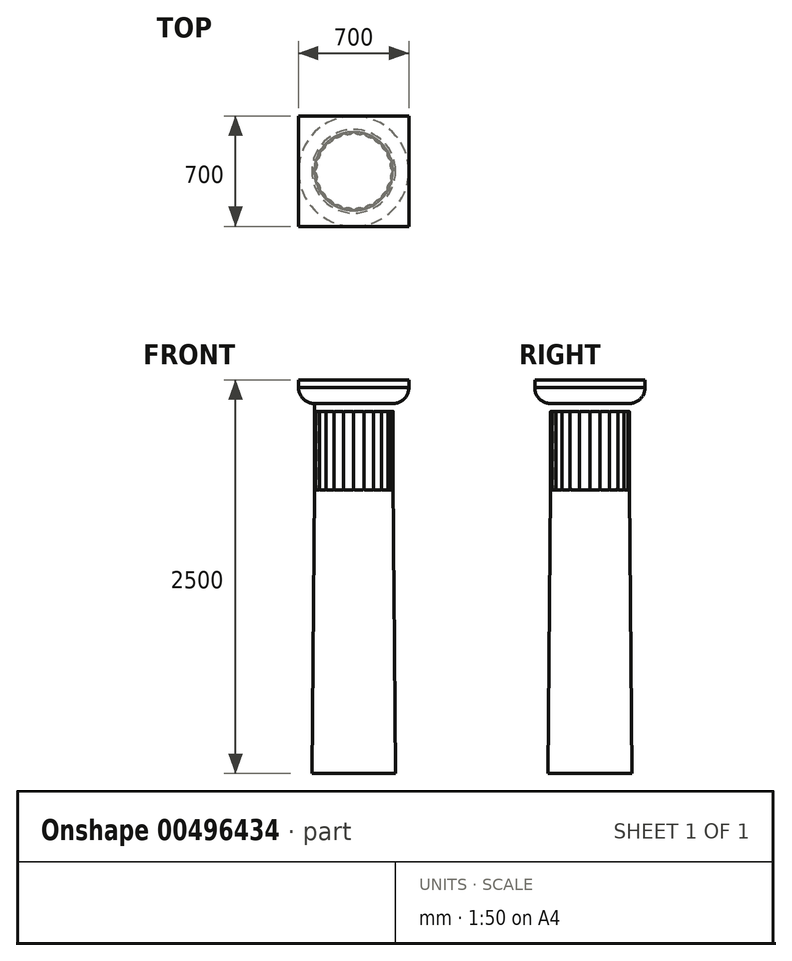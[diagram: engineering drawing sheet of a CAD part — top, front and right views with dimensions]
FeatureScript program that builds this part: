
annotation { "Feature Type Name" : "Feature", "Feature Type Description" : "" }
export const myFeature = defineFeature(function(context is Context, id is Id, definition is map)
    precondition{}
    {
        {
            var Q0;
            Q0=qCreatedBy(makeId("Top.planeOp"),FACE);
            var sketch = newSketch(context, id + "F0", { "sketchPlane" : qUnion([Q0])});
            skCircle(sketch, "E0", {"center": v(0, 0) * mm, "radius": 250 * mm});
            skArc(sketch, "E1", {"start": v(64.7, -241.48) * mm, "mid": v(30.88, -234.52) * mm, "end": v(0, -250) * mm});
            skLineSegment(sketch, "E2", {"start": v(0, 0) * mm, "end": v(30.88, -234.52) * mm, "construction": true});
            skLineSegment(sketch, "E3", {"start": v(30.88, -234.52) * mm, "end": v(32.63, -247.86) * mm, "construction": true});
            skArc(sketch, "E4.1.0", {"start": v(125, -216.5) * mm, "mid": v(90.52, -218.54) * mm, "end": v(64.7, -241.48) * mm});
            skArc(sketch, "E4.2.0", {"start": v(176.78, -176.78) * mm, "mid": v(144, -187.66) * mm, "end": v(125, -216.5) * mm});
            skArc(sketch, "E4.3.0", {"start": v(216.5, -125) * mm, "mid": v(187.66, -144) * mm, "end": v(176.78, -176.78) * mm});
            skArc(sketch, "E4.4.0", {"start": v(241.48, -64.7) * mm, "mid": v(218.54, -90.52) * mm, "end": v(216.5, -125) * mm});
            skArc(sketch, "E4.5.0", {"start": v(250, 0) * mm, "mid": v(234.52, -30.88) * mm, "end": v(241.48, -64.7) * mm});
            skArc(sketch, "E4.6.0", {"start": v(241.48, 64.7) * mm, "mid": v(234.52, 30.88) * mm, "end": v(250, 0) * mm});
            skArc(sketch, "E4.7.0", {"start": v(216.5, 125) * mm, "mid": v(218.54, 90.52) * mm, "end": v(241.48, 64.7) * mm});
            skArc(sketch, "E4.8.0", {"start": v(176.78, 176.78) * mm, "mid": v(187.66, 144) * mm, "end": v(216.5, 125) * mm});
            skArc(sketch, "E4.9.0", {"start": v(125, 216.5) * mm, "mid": v(144, 187.66) * mm, "end": v(176.78, 176.78) * mm});
            skArc(sketch, "E4.10.0", {"start": v(64.7, 241.48) * mm, "mid": v(90.52, 218.54) * mm, "end": v(125, 216.5) * mm});
            skArc(sketch, "E4.11.0", {"start": v(0, 250) * mm, "mid": v(30.88, 234.52) * mm, "end": v(64.7, 241.48) * mm});
            skArc(sketch, "E4.12.0", {"start": v(-64.7, 241.48) * mm, "mid": v(-30.88, 234.52) * mm, "end": v(0, 250) * mm});
            skArc(sketch, "E4.13.0", {"start": v(-125, 216.5) * mm, "mid": v(-90.52, 218.54) * mm, "end": v(-64.7, 241.48) * mm});
            skArc(sketch, "E4.14.0", {"start": v(-176.78, 176.78) * mm, "mid": v(-144, 187.66) * mm, "end": v(-125, 216.5) * mm});
            skArc(sketch, "E4.15.0", {"start": v(-216.5, 125) * mm, "mid": v(-187.66, 144) * mm, "end": v(-176.78, 176.78) * mm});
            skArc(sketch, "E4.16.0", {"start": v(-241.48, 64.7) * mm, "mid": v(-218.54, 90.52) * mm, "end": v(-216.5, 125) * mm});
            skArc(sketch, "E4.17.0", {"start": v(-250, 0) * mm, "mid": v(-234.52, 30.88) * mm, "end": v(-241.48, 64.7) * mm});
            skArc(sketch, "E4.18.0", {"start": v(-241.48, -64.7) * mm, "mid": v(-234.52, -30.88) * mm, "end": v(-250, 0) * mm});
            skArc(sketch, "E4.19.0", {"start": v(-216.5, -125) * mm, "mid": v(-218.54, -90.52) * mm, "end": v(-241.48, -64.7) * mm});
            skArc(sketch, "E4.20.0", {"start": v(-176.78, -176.78) * mm, "mid": v(-187.66, -144) * mm, "end": v(-216.5, -125) * mm});
            skArc(sketch, "E4.21.0", {"start": v(-125, -216.5) * mm, "mid": v(-144, -187.66) * mm, "end": v(-176.78, -176.78) * mm});
            skArc(sketch, "E4.22.0", {"start": v(-64.7, -241.48) * mm, "mid": v(-90.52, -218.54) * mm, "end": v(-125, -216.5) * mm});
            skArc(sketch, "E4.23.0", {"start": v(0, -250) * mm, "mid": v(-30.88, -234.52) * mm, "end": v(-64.7, -241.48) * mm});
            skSolve(sketch);
        }
        {
            var Q0;
            Q0=makeQuery(id+"F0.imprint","IMPRINT",FACE,{"disambiguationData":[TD([[makeQuery(id+"F0.imprint","IMPRINT",EDGE,{"derivedFrom":sQuery(id+"F0.wireOp",EDGE,"E1")}),-1.0]])]});
            extrude(context, id + "F1", {"entities" : qUnion([Q0]), "depth" : 500 * mm});
        }
        {
            var Q0;
            Q0 = qSketchRegion(id + "F0", true);
            extrude(context, id + "F2", {"entities" : qUnion([Q0]), "operationType" : NewBodyOperationType.ADD, "oppositeDirection" : true, "depth" : 1800 * mm, "hasDraft" : true, "draftAngle" : .5 * degree});
        }
        {
            var Q0;
            Q0=makeQuery(id+"F1.opExtrude","CAP_FACE",FACE,{"disambiguationData":[OSD([sQuery(id+"F0.wireOp",EDGE,"E1"),sQuery(id+"F0.wireOp",EDGE,"E4.1.0"),sQuery(id+"F0.wireOp",EDGE,"E4.2.0"),sQuery(id+"F0.wireOp",EDGE,"E4.3.0"),sQuery(id+"F0.wireOp",EDGE,"E4.4.0"),sQuery(id+"F0.wireOp",EDGE,"E4.5.0"),sQuery(id+"F0.wireOp",EDGE,"E4.6.0"),sQuery(id+"F0.wireOp",EDGE,"E4.7.0"),sQuery(id+"F0.wireOp",EDGE,"E4.8.0"),sQuery(id+"F0.wireOp",EDGE,"E4.9.0"),sQuery(id+"F0.wireOp",EDGE,"E4.10.0"),sQuery(id+"F0.wireOp",EDGE,"E4.11.0"),sQuery(id+"F0.wireOp",EDGE,"E4.12.0"),sQuery(id+"F0.wireOp",EDGE,"E4.13.0"),sQuery(id+"F0.wireOp",EDGE,"E4.14.0"),sQuery(id+"F0.wireOp",EDGE,"E4.15.0"),sQuery(id+"F0.wireOp",EDGE,"E4.16.0"),sQuery(id+"F0.wireOp",EDGE,"E4.17.0"),sQuery(id+"F0.wireOp",EDGE,"E4.18.0"),sQuery(id+"F0.wireOp",EDGE,"E4.19.0"),sQuery(id+"F0.wireOp",EDGE,"E4.20.0"),sQuery(id+"F0.wireOp",EDGE,"E4.21.0"),sQuery(id+"F0.wireOp",EDGE,"E4.22.0"),sQuery(id+"F0.wireOp",EDGE,"E4.23.0")])],"isStart":false});
            var sketch = newSketch(context, id + "F3", { "sketchPlane" : qUnion([Q0])});
            skCircle(sketch, "E5.0", {"center": v(0, 0) * mm, "radius": 250 * mm});
            skSolve(sketch);
        }
        {
            var Q0;
            Q0 = qSketchRegion(id + "F3", true);
            extrude(context, id + "F4", {"entities" : qUnion([Q0]), "operationType" : NewBodyOperationType.ADD, "depth" : 50 * mm});
        }
        {
            var Q0;
            Q0=makeQuery(id+"F4.opExtrude","CAP_FACE",FACE,{"disambiguationData":[OSD([sQuery(id+"F3.wireOp",EDGE,"E5.0")])],"isStart":false});
            var sketch = newSketch(context, id + "F5", { "sketchPlane" : qUnion([Q0])});
            skCircle(sketch, "E6", {"center": v(0, 0) * mm, "radius": 350 * mm});
            skSolve(sketch);
        }
        {
            var Q0;
            Q0 = qSketchRegion(id + "F5", true);
            extrude(context, id + "F6", {"entities" : qUnion([Q0]), "operationType" : NewBodyOperationType.ADD, "depth" : 100 * mm});
        }
        {
            var Q0;
            Q0=makeQuery(id+"F6.opExtrude","CAP_EDGE",EDGE,{"disambiguationData":[OSD([sQuery(id+"F5.wireOp",EDGE,"E6")])],"isStart":true});
            fillet(context, id + "F7", {"entities" : qUnion([Q0]), "radius" : 100 * mm, "tangentPropagation" : true, "allowEdgeOverflow" : false});
        }
        {
            var Q0;
            Q0=makeQuery(id+"F1.opExtrude","CAP_EDGE",EDGE,{"disambiguationData":[OSD([sQuery(id+"F0.wireOp",EDGE,"E4.20.0")])],"isStart":false});
            var Q1;
            Q1=makeQuery(id+"F1.opExtrude","CAP_EDGE",EDGE,{"disambiguationData":[OSD([sQuery(id+"F0.wireOp",EDGE,"E4.19.0")])],"isStart":false});
            var Q2;
            Q2=makeQuery(id+"F1.opExtrude","CAP_EDGE",EDGE,{"disambiguationData":[OSD([sQuery(id+"F0.wireOp",EDGE,"E4.18.0")])],"isStart":false});
            var Q3;
            Q3=makeQuery(id+"F1.opExtrude","CAP_EDGE",EDGE,{"disambiguationData":[OSD([sQuery(id+"F0.wireOp",EDGE,"E4.17.0")])],"isStart":false});
            var Q4;
            Q4=makeQuery(id+"F1.opExtrude","CAP_EDGE",EDGE,{"disambiguationData":[OSD([sQuery(id+"F0.wireOp",EDGE,"E4.21.0")])],"isStart":false});
            var Q5;
            Q5=makeQuery(id+"F1.opExtrude","CAP_EDGE",EDGE,{"disambiguationData":[OSD([sQuery(id+"F0.wireOp",EDGE,"E4.22.0")])],"isStart":false});
            var Q6;
            Q6=makeQuery(id+"F1.opExtrude","CAP_EDGE",EDGE,{"disambiguationData":[OSD([sQuery(id+"F0.wireOp",EDGE,"E4.23.0")])],"isStart":false});
            var Q7;
            Q7=makeQuery(id+"F1.opExtrude","CAP_EDGE",EDGE,{"disambiguationData":[OSD([sQuery(id+"F0.wireOp",EDGE,"E1")])],"isStart":false});
            var Q8;
            Q8=makeQuery(id+"F1.opExtrude","CAP_EDGE",EDGE,{"disambiguationData":[OSD([sQuery(id+"F0.wireOp",EDGE,"E4.1.0")])],"isStart":false});
            var Q9;
            Q9=makeQuery(id+"F1.opExtrude","CAP_EDGE",EDGE,{"disambiguationData":[OSD([sQuery(id+"F0.wireOp",EDGE,"E4.2.0")])],"isStart":false});
            var Q10;
            Q10=makeQuery(id+"F1.opExtrude","CAP_EDGE",EDGE,{"disambiguationData":[OSD([sQuery(id+"F0.wireOp",EDGE,"E4.3.0")])],"isStart":false});
            var Q11;
            Q11=makeQuery(id+"F1.opExtrude","CAP_EDGE",EDGE,{"disambiguationData":[OSD([sQuery(id+"F0.wireOp",EDGE,"E4.4.0")])],"isStart":false});
            var Q12;
            Q12=makeQuery(id+"F1.opExtrude","CAP_EDGE",EDGE,{"disambiguationData":[OSD([sQuery(id+"F0.wireOp",EDGE,"E4.5.0")])],"isStart":false});
            var Q13;
            Q13=makeQuery(id+"F1.opExtrude","CAP_EDGE",EDGE,{"disambiguationData":[OSD([sQuery(id+"F0.wireOp",EDGE,"E4.6.0")])],"isStart":false});
            var Q14;
            Q14=makeQuery(id+"F1.opExtrude","CAP_EDGE",EDGE,{"disambiguationData":[OSD([sQuery(id+"F0.wireOp",EDGE,"E4.7.0")])],"isStart":false});
            var Q15;
            Q15=makeQuery(id+"F1.opExtrude","CAP_EDGE",EDGE,{"disambiguationData":[OSD([sQuery(id+"F0.wireOp",EDGE,"E4.8.0")])],"isStart":false});
            var Q16;
            Q16=makeQuery(id+"F1.opExtrude","CAP_EDGE",EDGE,{"disambiguationData":[OSD([sQuery(id+"F0.wireOp",EDGE,"E4.9.0")])],"isStart":false});
            var Q17;
            Q17=makeQuery(id+"F1.opExtrude","CAP_EDGE",EDGE,{"disambiguationData":[OSD([sQuery(id+"F0.wireOp",EDGE,"E4.10.0")])],"isStart":false});
            var Q18;
            Q18=makeQuery(id+"F1.opExtrude","CAP_EDGE",EDGE,{"disambiguationData":[OSD([sQuery(id+"F0.wireOp",EDGE,"E4.11.0")])],"isStart":false});
            var Q19;
            Q19=makeQuery(id+"F1.opExtrude","CAP_EDGE",EDGE,{"disambiguationData":[OSD([sQuery(id+"F0.wireOp",EDGE,"E4.12.0")])],"isStart":false});
            var Q20;
            Q20=makeQuery(id+"F1.opExtrude","CAP_EDGE",EDGE,{"disambiguationData":[OSD([sQuery(id+"F0.wireOp",EDGE,"E4.13.0")])],"isStart":false});
            var Q21;
            Q21=makeQuery(id+"F1.opExtrude","CAP_EDGE",EDGE,{"disambiguationData":[OSD([sQuery(id+"F0.wireOp",EDGE,"E4.14.0")])],"isStart":false});
            var Q22;
            Q22=makeQuery(id+"F1.opExtrude","CAP_EDGE",EDGE,{"disambiguationData":[OSD([sQuery(id+"F0.wireOp",EDGE,"E4.15.0")])],"isStart":false});
            var Q23;
            Q23=makeQuery(id+"F1.opExtrude","CAP_EDGE",EDGE,{"disambiguationData":[OSD([sQuery(id+"F0.wireOp",EDGE,"E4.16.0")])],"isStart":false});
            var Q24;
            Q24=makeQuery(id+"F1.opExtrude","CAP_EDGE",EDGE,{"disambiguationData":[OSD([sQuery(id+"F0.wireOp",EDGE,"E4.11.0")])],"isStart":true});
            var Q25;
            Q25=makeQuery(id+"F1.opExtrude","CAP_EDGE",EDGE,{"disambiguationData":[OSD([sQuery(id+"F0.wireOp",EDGE,"E4.12.0")])],"isStart":true});
            var Q26;
            Q26=makeQuery(id+"F1.opExtrude","CAP_EDGE",EDGE,{"disambiguationData":[OSD([sQuery(id+"F0.wireOp",EDGE,"E4.13.0")])],"isStart":true});
            var Q27;
            Q27=makeQuery(id+"F1.opExtrude","CAP_EDGE",EDGE,{"disambiguationData":[OSD([sQuery(id+"F0.wireOp",EDGE,"E4.14.0")])],"isStart":true});
            var Q28;
            Q28=makeQuery(id+"F1.opExtrude","CAP_EDGE",EDGE,{"disambiguationData":[OSD([sQuery(id+"F0.wireOp",EDGE,"E4.15.0")])],"isStart":true});
            var Q29;
            Q29=makeQuery(id+"F1.opExtrude","CAP_EDGE",EDGE,{"disambiguationData":[OSD([sQuery(id+"F0.wireOp",EDGE,"E4.16.0")])],"isStart":true});
            var Q30;
            Q30=makeQuery(id+"F1.opExtrude","CAP_EDGE",EDGE,{"disambiguationData":[OSD([sQuery(id+"F0.wireOp",EDGE,"E4.10.0")])],"isStart":true});
            var Q31;
            Q31=makeQuery(id+"F1.opExtrude","CAP_EDGE",EDGE,{"disambiguationData":[OSD([sQuery(id+"F0.wireOp",EDGE,"E4.9.0")])],"isStart":true});
            var Q32;
            Q32=makeQuery(id+"F1.opExtrude","CAP_EDGE",EDGE,{"disambiguationData":[OSD([sQuery(id+"F0.wireOp",EDGE,"E4.8.0")])],"isStart":true});
            var Q33;
            Q33=makeQuery(id+"F1.opExtrude","CAP_EDGE",EDGE,{"disambiguationData":[OSD([sQuery(id+"F0.wireOp",EDGE,"E4.7.0")])],"isStart":true});
            var Q34;
            Q34=makeQuery(id+"F1.opExtrude","CAP_EDGE",EDGE,{"disambiguationData":[OSD([sQuery(id+"F0.wireOp",EDGE,"E4.6.0")])],"isStart":true});
            var Q35;
            Q35=makeQuery(id+"F1.opExtrude","CAP_EDGE",EDGE,{"disambiguationData":[OSD([sQuery(id+"F0.wireOp",EDGE,"E4.5.0")])],"isStart":true});
            var Q36;
            Q36=makeQuery(id+"F1.opExtrude","CAP_EDGE",EDGE,{"disambiguationData":[OSD([sQuery(id+"F0.wireOp",EDGE,"E4.4.0")])],"isStart":true});
            var Q37;
            Q37=makeQuery(id+"F1.opExtrude","CAP_EDGE",EDGE,{"disambiguationData":[OSD([sQuery(id+"F0.wireOp",EDGE,"E4.3.0")])],"isStart":true});
            var Q38;
            Q38=makeQuery(id+"F1.opExtrude","CAP_EDGE",EDGE,{"disambiguationData":[OSD([sQuery(id+"F0.wireOp",EDGE,"E4.2.0")])],"isStart":true});
            var Q39;
            Q39=makeQuery(id+"F1.opExtrude","CAP_EDGE",EDGE,{"disambiguationData":[OSD([sQuery(id+"F0.wireOp",EDGE,"E4.1.0")])],"isStart":true});
            var Q40;
            Q40=makeQuery(id+"F1.opExtrude","CAP_EDGE",EDGE,{"disambiguationData":[OSD([sQuery(id+"F0.wireOp",EDGE,"E1")])],"isStart":true});
            var Q41;
            Q41=makeQuery(id+"F1.opExtrude","CAP_EDGE",EDGE,{"disambiguationData":[OSD([sQuery(id+"F0.wireOp",EDGE,"E4.23.0")])],"isStart":true});
            var Q42;
            Q42=makeQuery(id+"F1.opExtrude","CAP_EDGE",EDGE,{"disambiguationData":[OSD([sQuery(id+"F0.wireOp",EDGE,"E4.22.0")])],"isStart":true});
            var Q43;
            Q43=makeQuery(id+"F1.opExtrude","CAP_EDGE",EDGE,{"disambiguationData":[OSD([sQuery(id+"F0.wireOp",EDGE,"E4.21.0")])],"isStart":true});
            var Q44;
            Q44=makeQuery(id+"F1.opExtrude","CAP_EDGE",EDGE,{"disambiguationData":[OSD([sQuery(id+"F0.wireOp",EDGE,"E4.20.0")])],"isStart":true});
            var Q45;
            Q45=makeQuery(id+"F1.opExtrude","CAP_EDGE",EDGE,{"disambiguationData":[OSD([sQuery(id+"F0.wireOp",EDGE,"E4.19.0")])],"isStart":true});
            var Q46;
            Q46=makeQuery(id+"F1.opExtrude","CAP_EDGE",EDGE,{"disambiguationData":[OSD([sQuery(id+"F0.wireOp",EDGE,"E4.18.0")])],"isStart":true});
            var Q47;
            Q47=makeQuery(id+"F1.opExtrude","CAP_EDGE",EDGE,{"disambiguationData":[OSD([sQuery(id+"F0.wireOp",EDGE,"E4.17.0")])],"isStart":true});
            var Q48;
            Q48=makeQuery(id+"F1.opExtrude","CAP_EDGE",EDGE,{"disambiguationData":[OSD([sQuery(id+"F0.wireOp",EDGE,"E4.20.0")])],"isStart":true});
            var Q49;
            Q49=makeQuery(id+"F1.opExtrude","CAP_EDGE",EDGE,{"disambiguationData":[OSD([sQuery(id+"F0.wireOp",EDGE,"E4.19.0")])],"isStart":true});
            var Q50;
            Q50=makeQuery(id+"F1.opExtrude","CAP_EDGE",EDGE,{"disambiguationData":[OSD([sQuery(id+"F0.wireOp",EDGE,"E4.18.0")])],"isStart":true});
            var Q51;
            Q51=makeQuery(id+"F1.opExtrude","CAP_EDGE",EDGE,{"disambiguationData":[OSD([sQuery(id+"F0.wireOp",EDGE,"E4.17.0")])],"isStart":true});
            fillet(context, id + "F8", {"entities" : qUnion([Q0, Q1, Q2, Q3, Q4, Q5, Q6, Q7, Q8, Q9, Q10, Q11, Q12, Q13, Q14, Q15, Q16, Q17, Q18, Q19, Q20, Q21, Q22, Q23, Q24, Q25, Q26, Q27, Q28, Q29, Q30, Q31, Q32, Q33, Q34, Q35, Q36, Q37, Q38, Q39, Q40, Q41, Q42, Q43, Q44, Q45, Q46, Q47, Q48, Q49, Q50, Q51]), "radius" : 12 * mm, "tangentPropagation" : true, "rho" : 0.6, "crossSection" : FilletCrossSection.CONIC, "allowEdgeOverflow" : false});
        }
        {
            var Q0;
            Q0=makeQuery(id+"F6.opExtrude","CAP_FACE",FACE,{"disambiguationData":[OSD([sQuery(id+"F5.wireOp",EDGE,"E6")])],"isStart":false});
            var sketch = newSketch(context, id + "F9", { "sketchPlane" : qUnion([Q0])});
            skLineSegment(sketch, "E7.bottom", {"start": v(350, -350) * mm, "end": v(-350, -350) * mm});
            skLineSegment(sketch, "E7.top", {"start": v(350, 350) * mm, "end": v(-350, 350) * mm});
            skLineSegment(sketch, "E7.left", {"start": v(350, -350) * mm, "end": v(350, 350) * mm});
            skLineSegment(sketch, "E7.right", {"start": v(-350, -350) * mm, "end": v(-350, 350) * mm});
            skPoint(sketch, "E7.middle", {"position": v(0, 0) * mm});
            skSolve(sketch);
        }
        {
            var Q0;
            Q0 = qSketchRegion(id + "F9", true);
            extrude(context, id + "F10", {"entities" : qUnion([Q0]), "operationType" : NewBodyOperationType.ADD, "depth" : 50 * mm});
        }
    });
